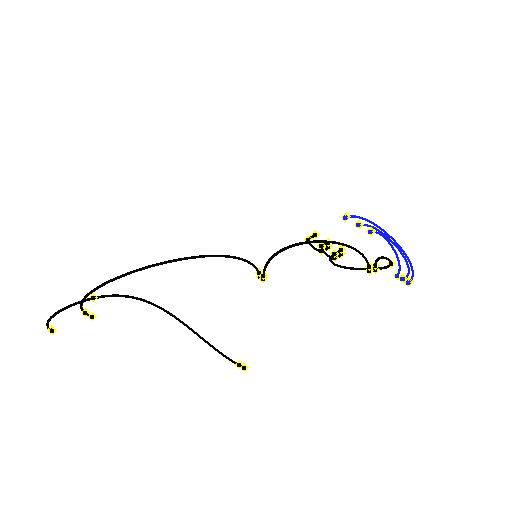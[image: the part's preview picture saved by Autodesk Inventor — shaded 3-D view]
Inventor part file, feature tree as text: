
AUTODESK INVENTOR PART (.ipt)
format: ipt  version: 2022 (Build 260153000, 153)  size: 787,968 bytes
history: native  units: mm (DEFAULTED — no unit token found)
features: other x56, plane x9, sketch x9, sweep x9
ambient origin geometry x8: Origin, YZ Plane, XZ Plane, XY Plane, X Axis, Y Axis, Z Axis, Center Point
bodies: Body1 (feature_tree), Body2 (feature_tree), Body3 (feature_tree), Body4 (feature_tree), Body5 (feature_tree), Body6 (feature_tree), Body7 (feature_tree), Body8 (feature_tree), Body9 (feature_tree)
feature tree (83):
  other  "Work Point1"
  other  "Work Point2"
  other  "Wire1"
  other  "Work Point3"
  other  "Work Point4"
  plane  "Work Plane1"
  other  "Work Point5"
  other  "Work Point6"
  other  "Wire2"
  other  "Work Point7"
  other  "Work Point8"
  plane  "Work Plane2"
  other  "Work Point9"
  other  "Work Point10"
  other  "Wire3"
  other  "Work Point11"
  other  "Work Point12"
  other  "Work Point13"
  plane  "Work Plane3"
  other  "Work Point14"
  other  "Work Point15"
  other  "Wire4"
  other  "Work Point16"
  other  "Work Point17"
  other  "Wire5"
  other  "Work Point18"
  other  "Work Point19"
  other  "Wire6"
  other  "Work Point20"
  other  "Work Point21"
  other  "Work Point22"
  other  "Work Point23"
  other  "Work Point24"
  other  "Work Point25"
  other  "Work Point26"
  plane  "Work Plane4"
  plane  "Work Plane5"
  plane  "Work Plane6"
  other  "Work Point27"
  other  "Work Point28"
  other  "Wire7"
  plane  "Work Plane7"
  other  "Work Point29"
  other  "Work Point30"
  other  "Wire8"
  other  "Work Point31"
  other  "Work Point32"
  other  "Wire9"
  plane  "Work Plane8"
  plane  "Work Plane9"
  other  "Work Point33"
  other  "Work Point34"
  other  "Work Point35"
  other  "Work Point36"
  other  "Work Point37"
  other  "Work Point38"
  sketch  "Sketch1"  dims[d0=0.0mm d1=0.0mm d2=0.0mm d3=0.0mm]
  other  "Srf1"
  sketch  "Sketch2"  dims[d4=0.0mm d5=0.0mm d6=0.0mm d7=0.0mm]
  other  "Srf2"
  sketch  "Sketch3"  dims[d8=0.0mm d9=0.0mm d10=0.0mm d11=0.0mm]
  other  "Srf3"
  sketch  "Sketch4"  dims[d12=0.0mm d13=0.0mm d14=0.0mm d15=0.0mm]
  other  "Srf4"
  sketch  "Sketch5"  dims[d16=0.0mm d17=0.0mm]
  other  "Srf5"
  sketch  "Sketch6"
  other  "Srf6"
  sketch  "Sketch7"
  other  "Srf7"
  sketch  "Sketch8"
  other  "Srf8"
  sketch  "Sketch9"
  other  "Srf9"
  sweep  "SweepSrf1"
  sweep  "SweepSrf2"
  sweep  "SweepSrf3"
  sweep  "SweepSrf4"
  sweep  "SweepSrf5"
  sweep  "SweepSrf6"
  sweep  "SweepSrf7"
  sweep  "SweepSrf8"
  sweep  "SweepSrf9"
